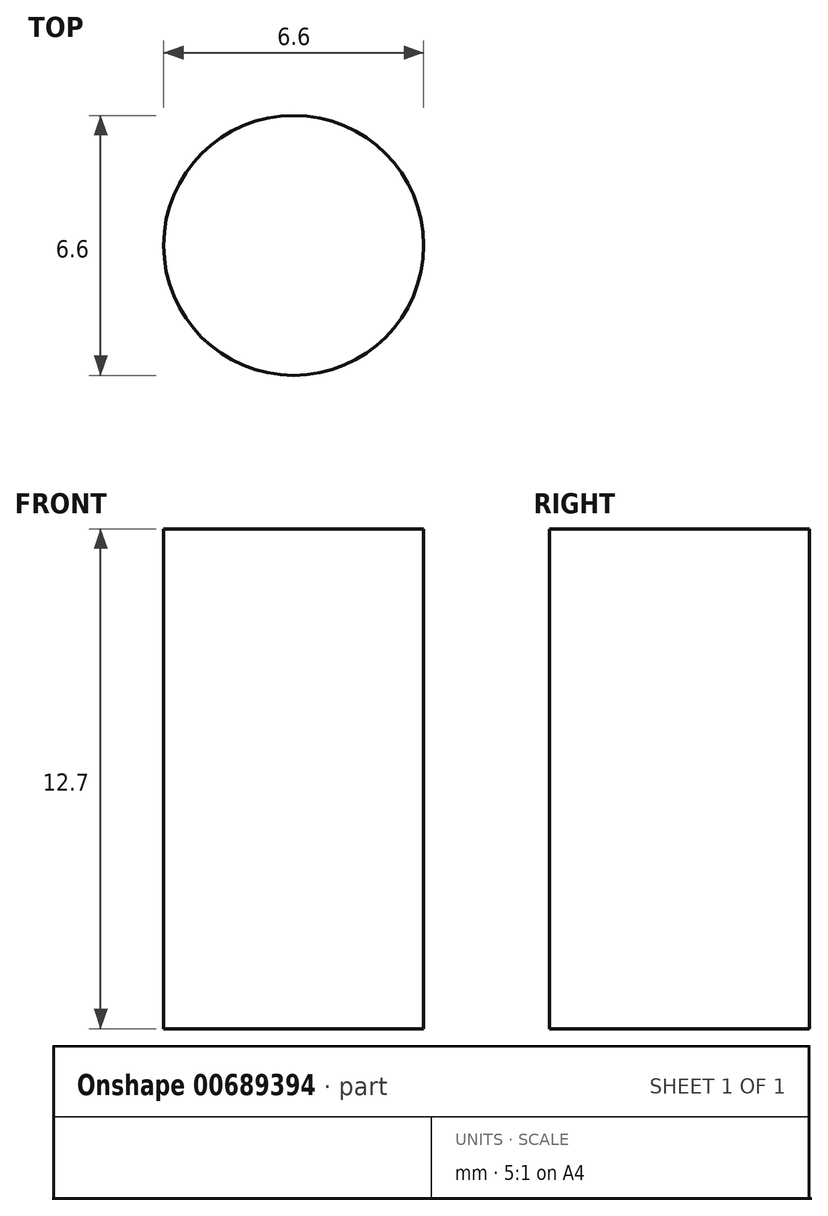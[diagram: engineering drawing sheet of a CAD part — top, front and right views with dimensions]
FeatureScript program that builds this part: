
annotation { "Feature Type Name" : "Feature", "Feature Type Description" : "" }
export const myFeature = defineFeature(function(context is Context, id is Id, definition is map)
    precondition{}
    {
        {
            var Q0;
            Q0=qCreatedBy(makeId("Top.planeOp"),FACE);
            var sketch = newSketch(context, id + "F0", { "sketchPlane" : qUnion([Q0])});
            skCircle(sketch, "E0", {"center": v(0, 0) * mm, "radius": 3.3 * mm});
            skSolve(sketch);
        }
        {
            var Q0;
            Q0 = qSketchRegion(id + "F0", true);
            extrude(context, id + "F1", {"entities" : qUnion([Q0]), "depth" : 12.7 * mm, "offsetDistance" : 25.4 * mm});
        }
    });
